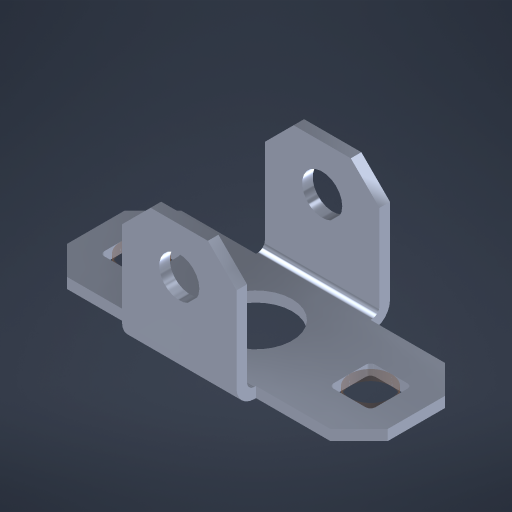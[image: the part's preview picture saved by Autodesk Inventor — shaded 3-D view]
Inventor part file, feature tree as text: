
AUTODESK INVENTOR PART (.ipt)
format: ipt  version: 2024 (Build 280153000, 153)  size: 290,816 bytes
history: native  units: in
note: dims shown in document units (in); Inventor stores cm internally (conversion verified against a paired STEP export)
features: other x3, extrude x2, chamfer x1, sketch x1, imported_body x1
ambient origin geometry x8: Origin, YZ Plane, XZ Plane, XY Plane, X Axis, Y Axis, Z Axis, Center Point
bodies: Body1 (feature_tree), Body2 (feature_tree), Body3 (feature_tree)
feature tree (8):
  chamfer  "Chamfer1"  Distance=1.0in
  other  "VL-PNEU-PVT-0011"
  sketch  "Sketch1"  dims[d2=1.0in d3=0.0in]
  imported_body  "Base1"
  other  "Srf1"
  other  "Srf2"
  extrude  "ExtrusionSrf1"  [1 undecoded]
  extrude  "ExtrusionSrf2"  [1 undecoded]
note: 2 required parameter values undecoded (feature->parameter linkage not recoverable at this tier; creation-order binding heuristic only, values carry confidence <= 0.55)
